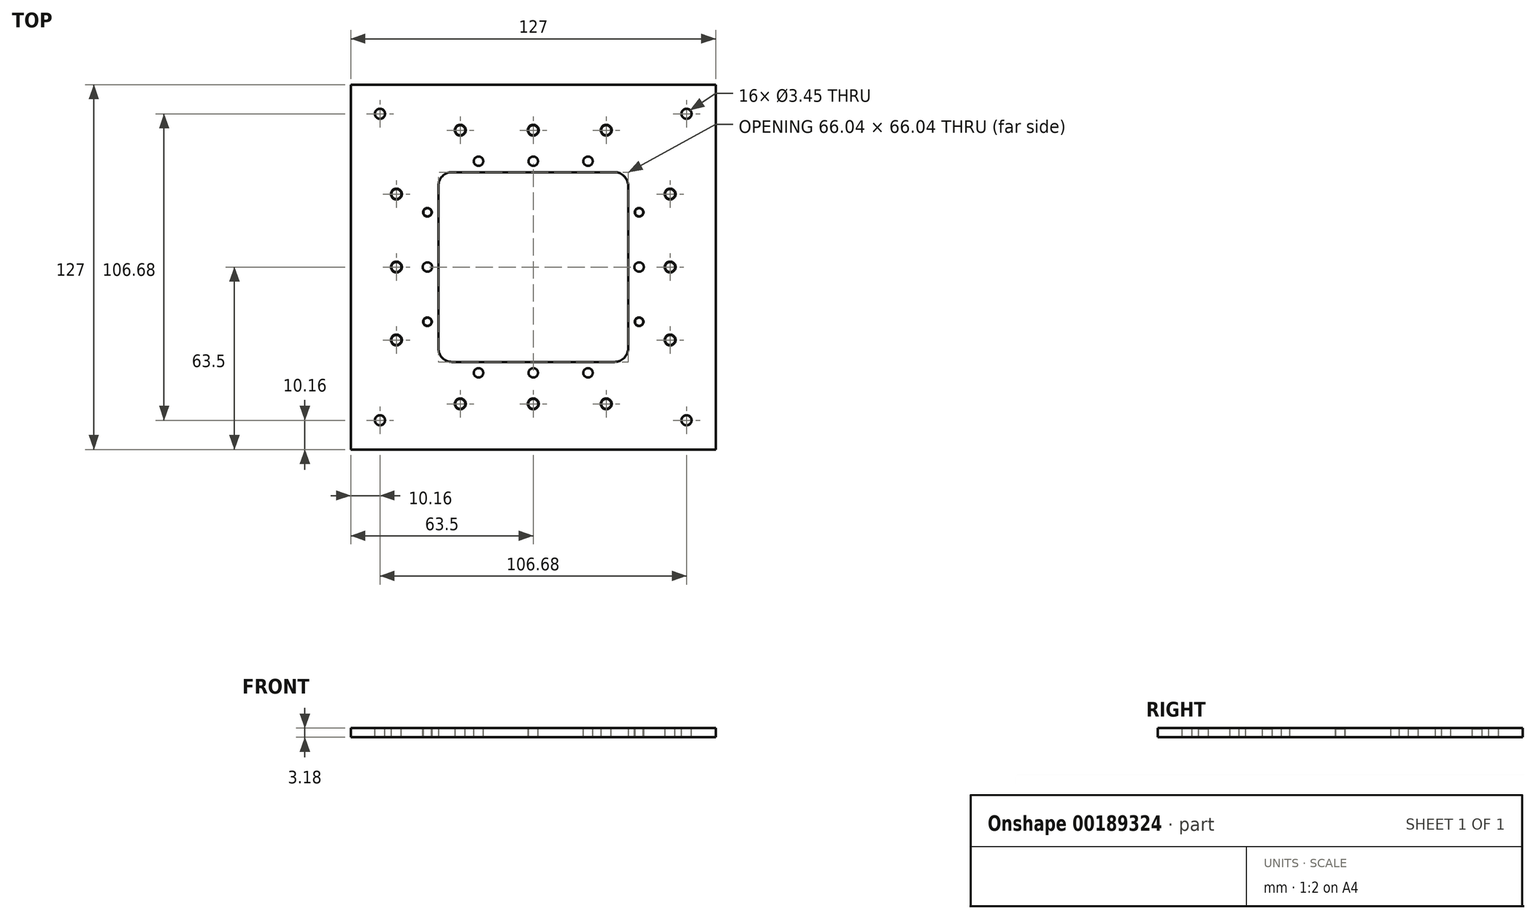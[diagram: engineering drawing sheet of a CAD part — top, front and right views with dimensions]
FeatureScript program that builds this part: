
annotation { "Feature Type Name" : "Feature", "Feature Type Description" : "" }
export const myFeature = defineFeature(function(context is Context, id is Id, definition is map)
    precondition{}
    {
        {
            var Q0;
            Q0=qCreatedBy(makeId("Top.planeOp"),FACE);
            var sketch = newSketch(context, id + "F0", { "sketchPlane" : qUnion([Q0])});
            skLineSegment(sketch, "E0.bottom", {"start": v(63.5, 63.5) * mm, "end": v(-63.5, 63.5) * mm});
            skLineSegment(sketch, "E0.top", {"start": v(63.5, -63.5) * mm, "end": v(-63.5, -63.5) * mm});
            skLineSegment(sketch, "E0.left", {"start": v(63.5, 63.5) * mm, "end": v(63.5, -63.5) * mm});
            skLineSegment(sketch, "E0.right", {"start": v(-63.5, 63.5) * mm, "end": v(-63.5, -63.5) * mm});
            skPoint(sketch, "E0.middle", {"position": v(0, 0) * mm});
            skLineSegment(sketch, "E1.bottom", {"start": v(28.26, 33.02) * mm, "end": v(-28.26, 33.02) * mm});
            skLineSegment(sketch, "E1.top", {"start": v(28.26, -33.02) * mm, "end": v(-28.26, -33.02) * mm});
            skLineSegment(sketch, "E1.left", {"start": v(33.02, 28.26) * mm, "end": v(33.02, -28.26) * mm});
            skLineSegment(sketch, "E1.right", {"start": v(-33.02, 28.26) * mm, "end": v(-33.02, -28.26) * mm});
            skPoint(sketch, "E2.visualSharp", {"position": v(-33.02, 33.02) * mm});
            skArc(sketch, "E2.filletArc", {"start": v(-28.26, 33.02) * mm, "mid": v(-31.63, 31.63) * mm, "end": v(-33.02, 28.26) * mm});
            skPoint(sketch, "E3.visualSharp", {"position": v(-33.02, -33.02) * mm});
            skArc(sketch, "E3.filletArc", {"start": v(-33.02, -28.26) * mm, "mid": v(-31.63, -31.63) * mm, "end": v(-28.26, -33.02) * mm});
            skPoint(sketch, "E4.visualSharp", {"position": v(33.02, -33.02) * mm});
            skArc(sketch, "E4.filletArc", {"start": v(28.26, -33.02) * mm, "mid": v(31.63, -31.63) * mm, "end": v(33.02, -28.26) * mm});
            skPoint(sketch, "E5.visualSharp", {"position": v(33.02, 33.02) * mm});
            skArc(sketch, "E5.filletArc", {"start": v(33.02, 28.26) * mm, "mid": v(31.63, 31.63) * mm, "end": v(28.26, 33.02) * mm});
            skSolve(sketch);
        }
        {
            var Q0;
            Q0=makeQuery(id+"F0.imprint","IMPRINT",FACE,{"disambiguationData":[TD([[makeQuery(id+"F0.imprint","IMPRINT",EDGE,{"derivedFrom":sQuery(id+"F0.wireOp",EDGE,"E0.bottom")}),1.0]])]});
            extrude(context, id + "F1", {"entities" : qUnion([Q0]), "depth" : 3.17 * mm});
        }
        {
            var Q0;
            Q0=makeQuery(id+"F1.opExtrude","CAP_FACE",FACE,{"disambiguationData":[OSD([sQuery(id+"F0.wireOp",EDGE,"E0.bottom"),sQuery(id+"F0.wireOp",EDGE,"E0.top"),sQuery(id+"F0.wireOp",EDGE,"E0.left"),sQuery(id+"F0.wireOp",EDGE,"E0.right"),sQuery(id+"F0.wireOp",EDGE,"E1.bottom"),sQuery(id+"F0.wireOp",EDGE,"E1.top"),sQuery(id+"F0.wireOp",EDGE,"E1.left"),sQuery(id+"F0.wireOp",EDGE,"E1.right"),sQuery(id+"F0.wireOp",EDGE,"E2.filletArc"),sQuery(id+"F0.wireOp",EDGE,"E3.filletArc"),sQuery(id+"F0.wireOp",EDGE,"E4.filletArc"),sQuery(id+"F0.wireOp",EDGE,"E5.filletArc")])],"isStart":false});
            var sketch = newSketch(context, id + "F2", { "sketchPlane" : qUnion([Q0])});
            skPoint(sketch, "E6", {"position": v(-53.34, 53.34) * mm});
            skPoint(sketch, "E7", {"position": v(-19.05, 36.83) * mm});
            skPoint(sketch, "E8", {"position": v(25.4, 47.62) * mm});
            skPoint(sketch, "E9.0.1.0", {"position": v(25.4, -47.63) * mm});
            skPoint(sketch, "E9.1.0.0", {"position": v(0, 47.62) * mm});
            skPoint(sketch, "E9.1.1.0", {"position": v(0, -47.63) * mm});
            skPoint(sketch, "E9.2.0.0", {"position": v(-25.4, 47.62) * mm});
            skPoint(sketch, "E9.2.1.0", {"position": v(-25.4, -47.63) * mm});
            skLineSegment(sketch, "E9.direction1", {"start": v(25.4, 47.62) * mm, "end": v(0, 47.62) * mm, "construction": true});
            skLineSegment(sketch, "E9.direction2", {"start": v(25.4, 47.62) * mm, "end": v(25.4, -47.63) * mm, "construction": true});
            skPoint(sketch, "E10.0.1.0", {"position": v(-19.05, -36.83) * mm});
            skPoint(sketch, "E10.1.0.0", {"position": v(0, 36.83) * mm});
            skPoint(sketch, "E10.1.1.0", {"position": v(0, -36.83) * mm});
            skPoint(sketch, "E10.2.0.0", {"position": v(19.05, 36.83) * mm});
            skPoint(sketch, "E10.2.1.0", {"position": v(19.05, -36.83) * mm});
            skLineSegment(sketch, "E10.direction1", {"start": v(-19.05, 36.83) * mm, "end": v(0, 36.83) * mm, "construction": true});
            skLineSegment(sketch, "E10.direction2", {"start": v(-19.05, 36.83) * mm, "end": v(-19.05, -36.83) * mm, "construction": true});
            skPoint(sketch, "E11", {"position": v(-36.83, 19.05) * mm});
            skPoint(sketch, "E12.0.1.0", {"position": v(-36.83, 0) * mm});
            skPoint(sketch, "E12.0.2.0", {"position": v(-36.83, -19.05) * mm});
            skPoint(sketch, "E12.1.0.0", {"position": v(36.83, 19.05) * mm});
            skPoint(sketch, "E12.1.1.0", {"position": v(36.83, 0) * mm});
            skPoint(sketch, "E12.1.2.0", {"position": v(36.83, -19.05) * mm});
            skLineSegment(sketch, "E12.direction1", {"start": v(-36.83, 19.05) * mm, "end": v(36.83, 19.05) * mm, "construction": true});
            skLineSegment(sketch, "E12.direction2", {"start": v(-36.83, 19.05) * mm, "end": v(-36.83, 0) * mm, "construction": true});
            skPoint(sketch, "E13.0.1.0", {"position": v(-53.34, -53.34) * mm});
            skPoint(sketch, "E13.1.0.0", {"position": v(53.34, 53.34) * mm});
            skPoint(sketch, "E13.1.1.0", {"position": v(53.34, -53.34) * mm});
            skLineSegment(sketch, "E13.direction1", {"start": v(-53.34, 53.34) * mm, "end": v(53.34, 53.34) * mm, "construction": true});
            skLineSegment(sketch, "E13.direction2", {"start": v(-53.34, 53.34) * mm, "end": v(-53.34, -53.34) * mm, "construction": true});
            skPoint(sketch, "E14", {"position": v(-47.62, 25.4) * mm});
            skPoint(sketch, "E15.0.1.0", {"position": v(-47.62, 0) * mm});
            skPoint(sketch, "E15.0.2.0", {"position": v(-47.62, -25.4) * mm});
            skPoint(sketch, "E15.1.0.0", {"position": v(47.63, 25.4) * mm});
            skPoint(sketch, "E15.1.1.0", {"position": v(47.63, 0) * mm});
            skPoint(sketch, "E15.1.2.0", {"position": v(47.63, -25.4) * mm});
            skLineSegment(sketch, "E15.direction1", {"start": v(-47.62, 25.4) * mm, "end": v(47.63, 25.4) * mm, "construction": true});
            skLineSegment(sketch, "E15.direction2", {"start": v(-47.62, 25.4) * mm, "end": v(-47.62, 0) * mm, "construction": true});
            skSolve(sketch);
        }
        {
            var Q0;
            Q0=sQuery(id+"F2.wireOp",VERTEX,"E6");
            var Q1;
            Q1=sQuery(id+"F2.wireOp",VERTEX,"E13.1.0.0");
            var Q2;
            Q2=sQuery(id+"F2.wireOp",VERTEX,"E13.1.1.0");
            var Q3;
            Q3=sQuery(id+"F2.wireOp",VERTEX,"E13.0.1.0");
            var Q4;
            Q4=makeQuery(id+"F1.opExtrude","SWEPT_BODY",BODY,{"disambiguationData":[OSD([sQuery(id+"F0.wireOp",EDGE,"E0.bottom"),sQuery(id+"F0.wireOp",EDGE,"E0.top"),sQuery(id+"F0.wireOp",EDGE,"E0.left"),sQuery(id+"F0.wireOp",EDGE,"E0.right"),sQuery(id+"F0.wireOp",EDGE,"E1.bottom"),sQuery(id+"F0.wireOp",EDGE,"E1.top"),sQuery(id+"F0.wireOp",EDGE,"E1.left"),sQuery(id+"F0.wireOp",EDGE,"E1.right"),sQuery(id+"F0.wireOp",EDGE,"E2.filletArc"),sQuery(id+"F0.wireOp",EDGE,"E3.filletArc"),sQuery(id+"F0.wireOp",EDGE,"E4.filletArc"),sQuery(id+"F0.wireOp",EDGE,"E5.filletArc")])]});
            hole(context, id + "F3", {"style" : HoleStyle.C_SINK, "endStyle" : HoleEndStyle.THROUGH, "holeDiameter" : 3.45 * mm, "cSinkDiameter" : 3.56 * mm, "cSinkAngle" : 82 * degree, "locations" : qUnion([Q0, Q1, Q2, Q3]), "scope" : qUnion([Q4]), "isTappedThrough" : true});
        }
        {
            var Q0;
            Q0=sQuery(id+"F2.wireOp",VERTEX,"E9.2.0.0");
            var Q1;
            Q1=sQuery(id+"F2.wireOp",VERTEX,"E9.1.0.0");
            var Q2;
            Q2=sQuery(id+"F2.wireOp",VERTEX,"E8");
            var Q3;
            Q3=sQuery(id+"F2.wireOp",VERTEX,"E14");
            var Q4;
            Q4=sQuery(id+"F2.wireOp",VERTEX,"E15.0.1.0");
            var Q5;
            Q5=sQuery(id+"F2.wireOp",VERTEX,"E15.0.2.0");
            var Q6;
            Q6=sQuery(id+"F2.wireOp",VERTEX,"E9.2.1.0");
            var Q7;
            Q7=sQuery(id+"F2.wireOp",VERTEX,"E9.1.1.0");
            var Q8;
            Q8=sQuery(id+"F2.wireOp",VERTEX,"E9.0.1.0");
            var Q9;
            Q9=sQuery(id+"F2.wireOp",VERTEX,"E15.1.2.0");
            var Q10;
            Q10=sQuery(id+"F2.wireOp",VERTEX,"E15.1.1.0");
            var Q11;
            Q11=sQuery(id+"F2.wireOp",VERTEX,"E15.1.0.0");
            var Q12;
            Q12=makeQuery(id+"F1.opExtrude","SWEPT_BODY",BODY,{"disambiguationData":[OSD([sQuery(id+"F0.wireOp",EDGE,"E0.bottom"),sQuery(id+"F0.wireOp",EDGE,"E0.top"),sQuery(id+"F0.wireOp",EDGE,"E0.left"),sQuery(id+"F0.wireOp",EDGE,"E0.right"),sQuery(id+"F0.wireOp",EDGE,"E1.bottom"),sQuery(id+"F0.wireOp",EDGE,"E1.top"),sQuery(id+"F0.wireOp",EDGE,"E1.left"),sQuery(id+"F0.wireOp",EDGE,"E1.right"),sQuery(id+"F0.wireOp",EDGE,"E2.filletArc"),sQuery(id+"F0.wireOp",EDGE,"E3.filletArc"),sQuery(id+"F0.wireOp",EDGE,"E4.filletArc"),sQuery(id+"F0.wireOp",EDGE,"E5.filletArc")])]});
            hole(context, id + "F4", {"style" : HoleStyle.C_SINK, "endStyle" : HoleEndStyle.THROUGH, "holeDiameter" : 3.45 * mm, "cSinkDiameter" : 3.8 * mm, "cSinkAngle" : 82 * degree, "locations" : qUnion([Q0, Q1, Q2, Q3, Q4, Q5, Q6, Q7, Q8, Q9, Q10, Q11]), "scope" : qUnion([Q12]), "isTappedThrough" : true});
        }
        {
            var Q0;
            Q0=sQuery(id+"F2.wireOp",VERTEX,"E11");
            var Q1;
            Q1=sQuery(id+"F2.wireOp",VERTEX,"E12.0.2.0");
            var Q2;
            Q2=sQuery(id+"F2.wireOp",VERTEX,"E12.1.0.0");
            var Q3;
            Q3=sQuery(id+"F2.wireOp",VERTEX,"E12.1.2.0");
            var Q4;
            Q4=makeQuery(id+"F1.opExtrude","SWEPT_BODY",BODY,{"disambiguationData":[OSD([sQuery(id+"F0.wireOp",EDGE,"E0.bottom"),sQuery(id+"F0.wireOp",EDGE,"E0.top"),sQuery(id+"F0.wireOp",EDGE,"E0.left"),sQuery(id+"F0.wireOp",EDGE,"E0.right"),sQuery(id+"F0.wireOp",EDGE,"E1.bottom"),sQuery(id+"F0.wireOp",EDGE,"E1.top"),sQuery(id+"F0.wireOp",EDGE,"E1.left"),sQuery(id+"F0.wireOp",EDGE,"E1.right"),sQuery(id+"F0.wireOp",EDGE,"E2.filletArc"),sQuery(id+"F0.wireOp",EDGE,"E3.filletArc"),sQuery(id+"F0.wireOp",EDGE,"E4.filletArc"),sQuery(id+"F0.wireOp",EDGE,"E5.filletArc")])]});
            hole(context, id + "F5", {"style" : HoleStyle.C_SINK, "endStyle" : HoleEndStyle.THROUGH, "holeDiameter" : 2.84 * mm, "cSinkDiameter" : 3.05 * mm, "cSinkAngle" : 82 * degree, "locations" : qUnion([Q0, Q1, Q2, Q3]), "scope" : qUnion([Q4]), "isTappedThrough" : true});
        }
        {
            var Q0;
            Q0=sQuery(id+"F2.wireOp",VERTEX,"E12.0.1.0");
            var Q1;
            Q1=sQuery(id+"F2.wireOp",VERTEX,"E7");
            var Q2;
            Q2=sQuery(id+"F2.wireOp",VERTEX,"E10.1.0.0");
            var Q3;
            Q3=sQuery(id+"F2.wireOp",VERTEX,"E10.2.0.0");
            var Q4;
            Q4=sQuery(id+"F2.wireOp",VERTEX,"E12.1.1.0");
            var Q5;
            Q5=sQuery(id+"F2.wireOp",VERTEX,"E10.2.1.0");
            var Q6;
            Q6=sQuery(id+"F2.wireOp",VERTEX,"E10.1.1.0");
            var Q7;
            Q7=sQuery(id+"F2.wireOp",VERTEX,"E10.0.1.0");
            var Q8;
            Q8=makeQuery(id+"F1.opExtrude","SWEPT_BODY",BODY,{"disambiguationData":[OSD([sQuery(id+"F0.wireOp",EDGE,"E0.bottom"),sQuery(id+"F0.wireOp",EDGE,"E0.top"),sQuery(id+"F0.wireOp",EDGE,"E0.left"),sQuery(id+"F0.wireOp",EDGE,"E0.right"),sQuery(id+"F0.wireOp",EDGE,"E1.bottom"),sQuery(id+"F0.wireOp",EDGE,"E1.top"),sQuery(id+"F0.wireOp",EDGE,"E1.left"),sQuery(id+"F0.wireOp",EDGE,"E1.right"),sQuery(id+"F0.wireOp",EDGE,"E2.filletArc"),sQuery(id+"F0.wireOp",EDGE,"E3.filletArc"),sQuery(id+"F0.wireOp",EDGE,"E4.filletArc"),sQuery(id+"F0.wireOp",EDGE,"E5.filletArc")])]});
            hole(context, id + "F6", {"style" : HoleStyle.SIMPLE, "endStyle" : HoleEndStyle.THROUGH, "standardTappedOrClearance" : lookupTablePath({ "standard" : "ANSI", "fit" : "Normal (ASME)", "size" : "#4", "type" : "Clearance" }), "standardBlindInLast" : lookupTablePath({ "fit" : "Free", "standard" : "ANSI", "size" : "#4", "type" : "Clearance" }), "holeDiameter" : 3.26 * mm, "locations" : qUnion([Q0, Q1, Q2, Q3, Q4, Q5, Q6, Q7]), "scope" : qUnion([Q8]), "isTappedThrough" : true});
        }
    });
